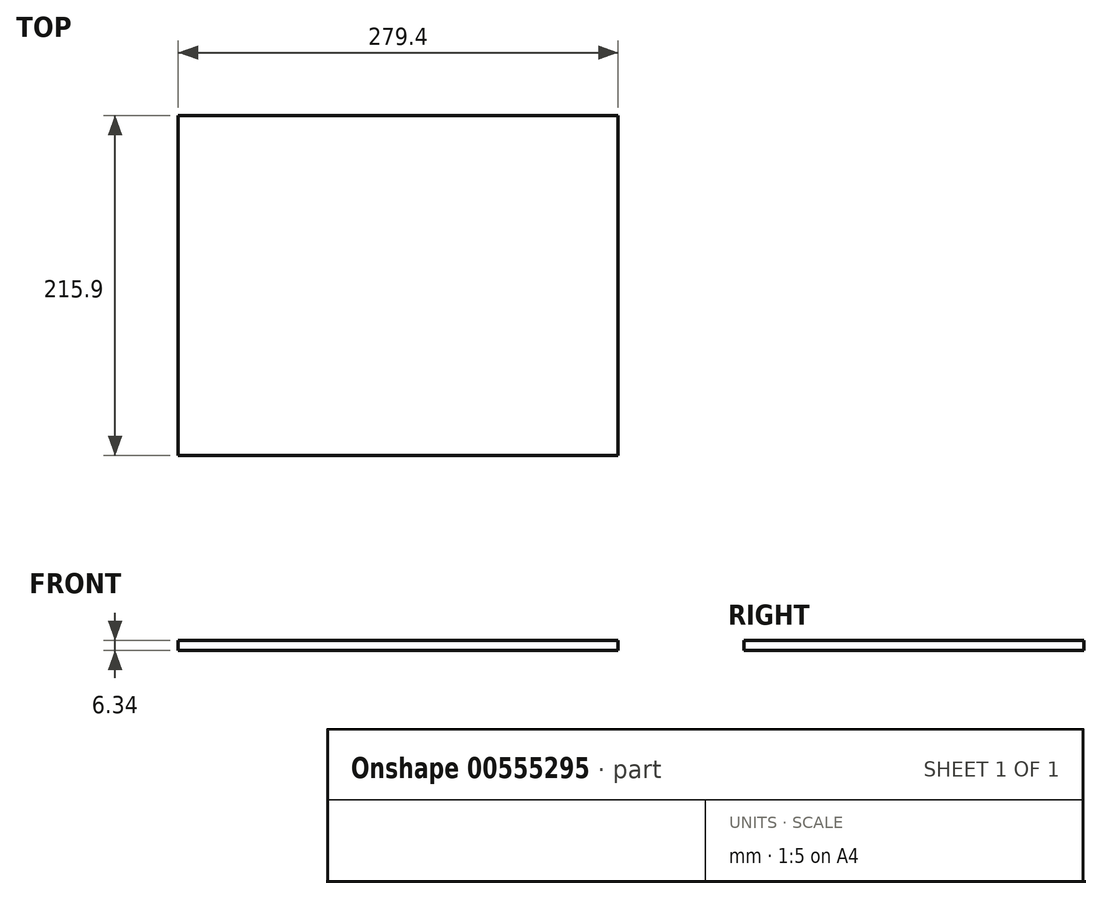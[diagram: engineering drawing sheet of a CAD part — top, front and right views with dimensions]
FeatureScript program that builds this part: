
annotation { "Feature Type Name" : "Feature", "Feature Type Description" : "" }
export const myFeature = defineFeature(function(context is Context, id is Id, definition is map)
    precondition{}
    {
        {
            var Q0;
            Q0=qCreatedBy(makeId("Top.planeOp"),FACE);
            var sketch = newSketch(context, id + "F0", { "sketchPlane" : qUnion([Q0])});
            skLineSegment(sketch, "E0.bottom", {"start": v(-139.7, 107.95) * mm, "end": v(139.7, 107.95) * mm});
            skLineSegment(sketch, "E0.top", {"start": v(-139.7, -107.95) * mm, "end": v(139.7, -107.95) * mm});
            skLineSegment(sketch, "E0.left", {"start": v(-139.7, 107.95) * mm, "end": v(-139.7, -107.95) * mm});
            skLineSegment(sketch, "E0.right", {"start": v(139.7, 107.95) * mm, "end": v(139.7, -107.95) * mm});
            skPoint(sketch, "E0.middle", {"position": v(0, 0) * mm});
            skSolve(sketch);
        }
        {
            var Q0;
            Q0=makeQuery(id+"F0.imprint","IMPRINT",FACE,{"disambiguationData":[TD([[makeQuery(id+"F0.imprint","IMPRINT",EDGE,{"derivedFrom":sQuery(id+"F0.wireOp",EDGE,"E0.bottom")}),-1.0]])]});
            extrude(context, id + "F1", {"entities" : qUnion([Q0]), "endBound" : BoundingType.SYMMETRIC, "depth" : 6.35 * mm, "offsetDistance" : 25.4 * mm});
        }
    });
